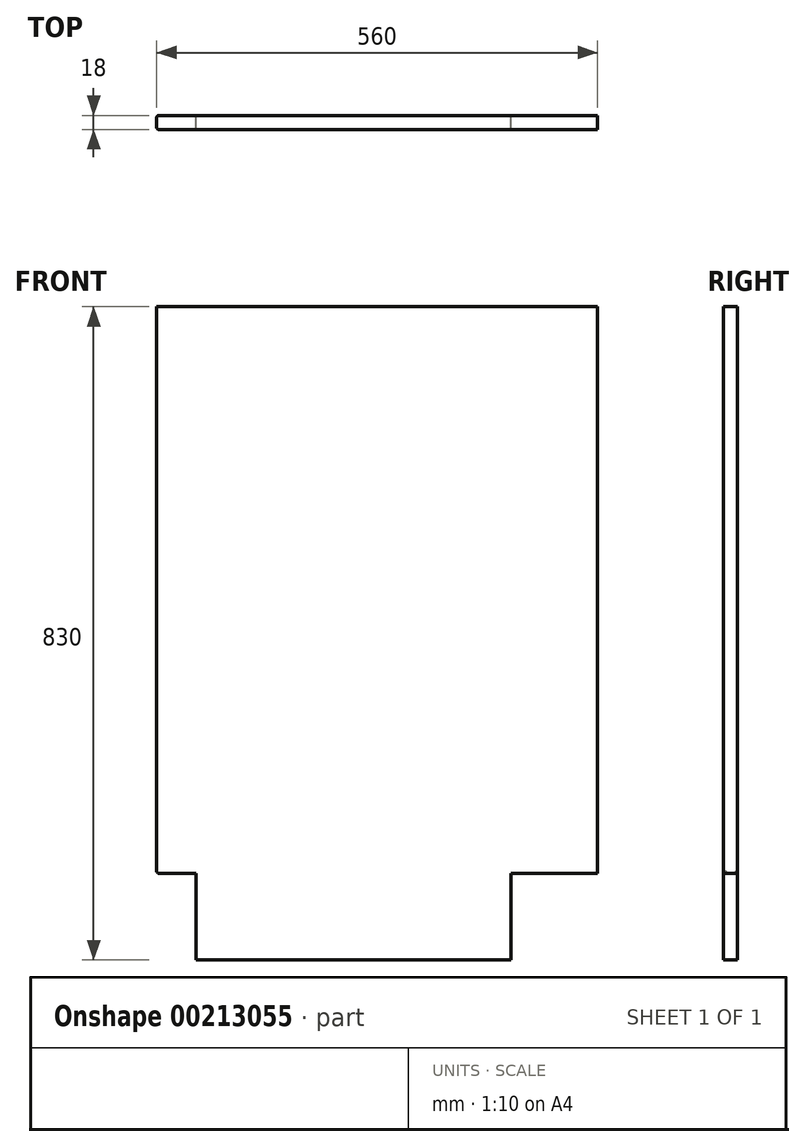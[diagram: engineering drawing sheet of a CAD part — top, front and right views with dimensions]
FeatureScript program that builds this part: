
annotation { "Feature Type Name" : "Feature", "Feature Type Description" : "" }
export const myFeature = defineFeature(function(context is Context, id is Id, definition is map)
    precondition{}
    {
        {
            var Q0;
            Q0=qCreatedBy(makeId("Front.planeOp"),FACE);
            var sketch = newSketch(context, id + "F0", { "sketchPlane" : qUnion([Q0])});
            skLineSegment(sketch, "E0.bottom", {"start": v(280, 415) * mm, "end": v(-280, 415) * mm});
            skLineSegment(sketch, "E0.left", {"start": v(280, 415) * mm, "end": v(280, -305) * mm});
            skLineSegment(sketch, "E0.right", {"start": v(-280, 415) * mm, "end": v(-280, -305) * mm});
            skPoint(sketch, "E0.middle", {"position": v(0, 0) * mm});
            skLineSegment(sketch, "E1.top", {"start": v(280, -305) * mm, "end": v(170, -305) * mm});
            skLineSegment(sketch, "E1.right", {"start": v(170, -415) * mm, "end": v(170, -305) * mm});
            skLineSegment(sketch, "E2.top", {"start": v(-280, -305) * mm, "end": v(-230, -305) * mm});
            skLineSegment(sketch, "E2.right", {"start": v(-230, -415) * mm, "end": v(-230, -305) * mm});
            skLineSegment(sketch, "E3", {"start": v(-230, -415) * mm, "end": v(170, -415) * mm});
            skSolve(sketch);
        }
        {
            var Q0;
            Q0=makeQuery(id+"F0.imprint","IMPRINT",FACE,{"disambiguationData":[TD([[makeQuery(id+"F0.imprint","IMPRINT",EDGE,{"derivedFrom":sQuery(id+"F0.wireOp",EDGE,"E0.bottom")}),1.0]])]});
            extrude(context, id + "F1", {"entities" : qUnion([Q0]), "endBound" : BoundingType.SYMMETRIC, "depth" : 18 * mm});
        }
        {
            var Q0;
            Q0=makeQuery(id+"F1.opExtrude","CAP_EDGE",EDGE,{"disambiguationData":[OSD([sQuery(id+"F0.wireOp",EDGE,"E0.right")])],"isStart":false});
            var Q1;
            Q1=makeQuery(id+"F1.opExtrude","CAP_EDGE",EDGE,{"disambiguationData":[OSD([sQuery(id+"F0.wireOp",EDGE,"E0.right")])],"isStart":true});
            var Q2;
            Q2=makeQuery(id+"F1.opExtrude","SWEPT_EDGE",EDGE,{"disambiguationData":[OSD([sQuery(id+"F0.wireOp",EDGE,"E0.right"),sQuery(id+"F0.wireOp",EDGE,"E2.top")])]});
            fillet(context, id + "F2", {"entities" : qUnion([Q0, Q1, Q2]), "radius" : 3 * mm, "tangentPropagation" : true, "allowEdgeOverflow" : false});
        }
    });
